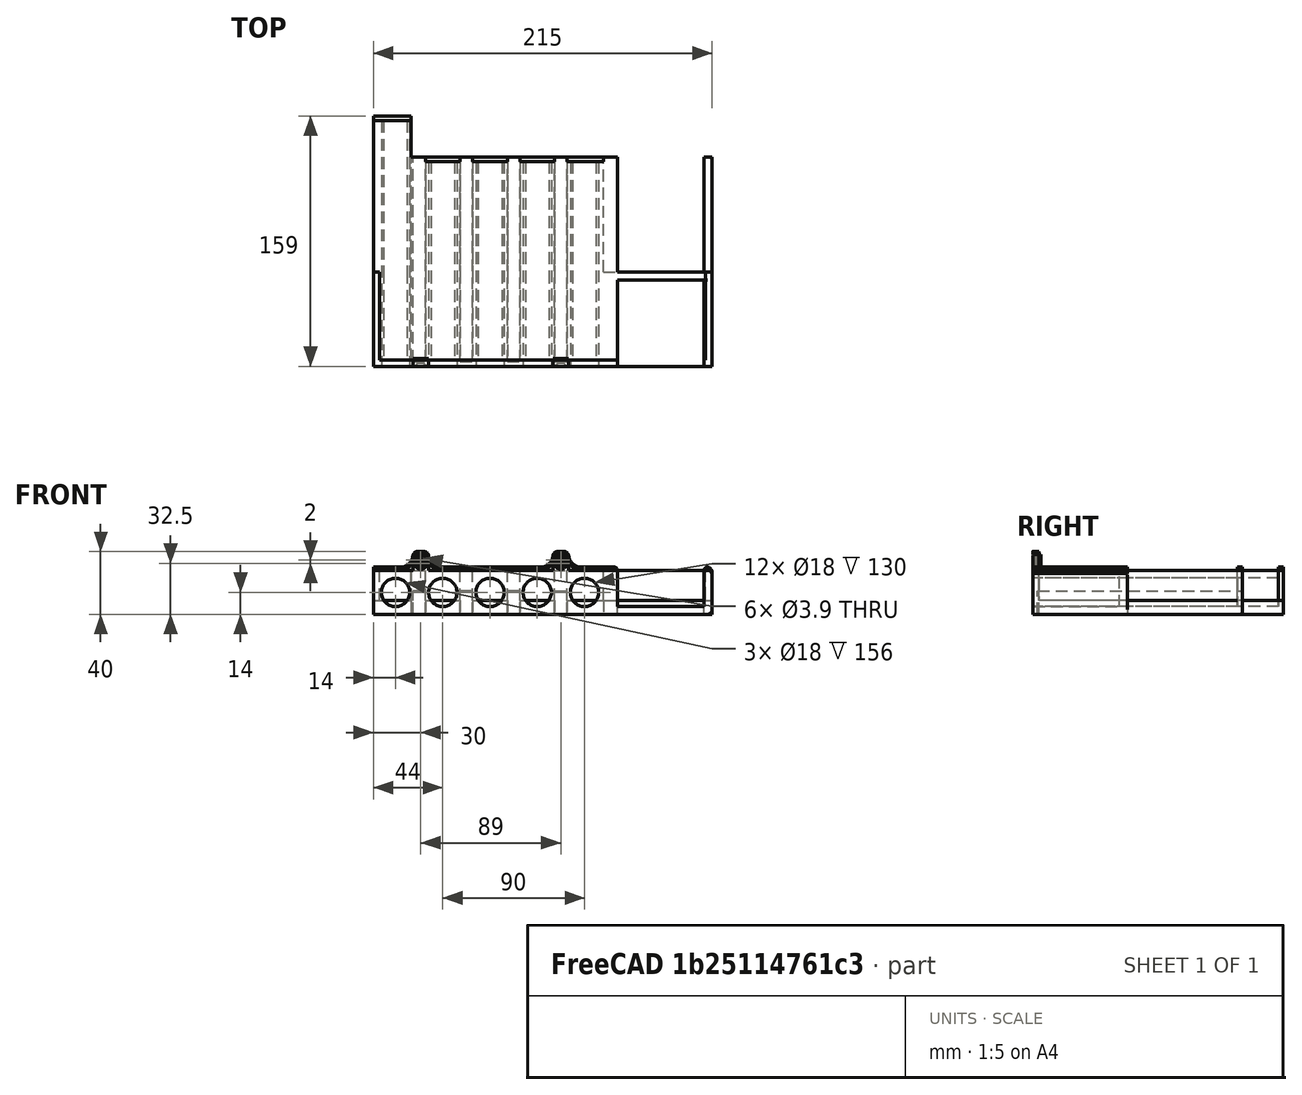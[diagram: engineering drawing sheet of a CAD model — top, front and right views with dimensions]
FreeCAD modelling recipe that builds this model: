
FCSTD DOCUMENT  (FreeCAD 0.20R29177 (Git))
Label: sujeta_lapices_cinta_metrica
License: All rights reserved
LicenseURL: http://en.wikipedia.org/wiki/All_rights_reserved
objects: Part::Box×19, Part::Cut×18, Part::Fillet×7, Part::Cylinder×5, Part::Feature×5, Part::MultiFuse×3, Sketcher::SketchObject×2, Mesh::Feature×2, PartDesign::Pad×1, PartDesign::Hole×1, PartDesign::Body×1, Part::Refine×1
note: 65 computed .brp shape members not serialized (recipe doc carries the construction recipe); baked Part::Feature solids carry a one-line shape summary decoded from their .brp

FEATURE [Part::Box] Box  label="Cube"
  AttacherType = Attacher::AttachEngine3D
  Height = 28
  Length = 215
  Width = 159
FEATURE [Part::Cylinder] Cylinder
  Angle = 360
  AttacherType = Attacher::AttachEngine3D
  FirstAngle = 0
  Height = 156
  Placement = pos=(14,156,14) rot=(1,0,0;1.5708rad)
  Radius = 9
  SecondAngle = 0
FEATURE [Part::Cylinder] Cylinder001 .. Cylinder004  x4 (patterned run collapsed; names and placements below)
  Angle = 360
  AttacherType = Attacher::AttachEngine3D
  FirstAngle = 0
  Height = 130
  Radius = 9
  SecondAngle = 0
  placements: 4 in arithmetic series — first pos=(44,130,14) rot=(1,0,0;1.5708rad), step (30,0,0), last pos=(134,130,14) rot=(1,0,0;1.5708rad)
FEATURE [Part::Box] Box001  label="Cube001"
  AttacherType = Attacher::AttachEngine3D
  Height = 23
  Length = 55
  Placement = pos=(155,0,5) rot=(0,0,1;0rad)
  Width = 55
FEATURE [Part::Box] Box002  label="Cube002"
  AttacherType = Attacher::AttachEngine3D
  Height = 34
  Length = 55
  Placement = pos=(155,60,-3) rot=(0,0,1;0rad)
  Width = 103
FEATURE [Part::Box] Box003  label="Cube003"
  AttacherType = Attacher::AttachEngine3D
  Height = 33
  Length = 197
  Placement = pos=(24,133,-3) rot=(0,0,1;0rad)
  Width = 103
FEATURE [Part::Box] Box004  label="Cube004"
  AttacherType = Attacher::AttachEngine3D
  Height = 15
  Length = 8
  Placement = pos=(25,3,0) rot=(0,0,1;0rad)
  Width = 165
FEATURE [Part::Box] Box005  label="Cube005"
  AttacherType = Attacher::AttachEngine3D
  Height = 15
  Length = 8
  Placement = pos=(55,3,0) rot=(0,0,1;0rad)
  Width = 165
FEATURE [Part::Box] Box006  label="Cube006"
  AttacherType = Attacher::AttachEngine3D
  Height = 15
  Length = 8
  Placement = pos=(85,3,0) rot=(0,0,1;0rad)
  Width = 165
FEATURE [Part::Box] Box007  label="Cube007"
  AttacherType = Attacher::AttachEngine3D
  Height = 15
  Length = 8
  Placement = pos=(115,3,0) rot=(0,0,1;0rad)
  Width = 165
FEATURE [Part::Cut] Cut
  Base = -> Box
  Tool = -> Box001
FEATURE [Part::Cut] Cut001
  Base = -> Cut
  Tool = -> Box002
FEATURE [Part::Cut] Cut002
  Base = -> Cut001
  Tool = -> Box003
FEATURE [Part::Cut] Cut003
  Base = -> Cut002
  Tool = -> Box004
FEATURE [Part::Cut] Cut004
  Base = -> Cut003
  Tool = -> Box005
FEATURE [Part::Cut] Cut005
  Base = -> Cut004
  Tool = -> Box006
FEATURE [Part::Cut] Cut006
  Base = -> Cut005
  Tool = -> Box007
FEATURE [Part::Cut] Cut007
  Base = -> Cut006
  Tool = -> Cylinder
FEATURE [Part::Cut] Cut008
  Base = -> Cut007
  Tool = -> Cylinder001
FEATURE [Part::Cut] Cut009
  Base = -> Cut008
  Tool = -> Cylinder002
FEATURE [Part::Cut] Cut010
  Base = -> Cut009
  Tool = -> Cylinder003
FEATURE [Part::Cut] Cut011
  Base = -> Cut010
  Tool = -> Cylinder004
FEATURE [Sketcher::SketchObject] Sketch
  FullyConstrained = true
  MapMode = 5
  Placement = pos=(0,0,0) rot=(1,0,0;1.5708rad)
  Support = -> [XZ_Plane]
  sketch-geometry (10):
    g0: LineSegment StartX=25 StartY=38 StartZ=0 EndX=35 EndY=38 EndZ=0
    g1: LineSegment StartX=35 StartY=38 StartZ=0 EndX=35 EndY=28 EndZ=0
    g2: LineSegment StartX=35 StartY=27 StartZ=0 EndX=25 EndY=27 EndZ=0
    g3: LineSegment StartX=25 StartY=27 StartZ=0 EndX=25 EndY=38 EndZ=0
    g4: LineSegment StartX=114 StartY=38 StartZ=0 EndX=124 EndY=38 EndZ=0
    g5: LineSegment StartX=124 StartY=38 StartZ=0 EndX=124 EndY=27 EndZ=0
    g6: LineSegment StartX=124 StartY=27 StartZ=0 EndX=114 EndY=27 EndZ=0
    g7: LineSegment StartX=114 StartY=28 StartZ=0 EndX=114 EndY=38 EndZ=0
    g8: LineSegment StartX=35 StartY=28 StartZ=0 EndX=114 EndY=28 EndZ=0
    g9: LineSegment StartX=114 StartY=27 StartZ=0 EndX=35 EndY=27 EndZ=0
  constraints (30):
    c: Coincident(g0,g1)
    c: Coincident(g2,g3)
    c: Coincident(g3,g0)
    c: Horizontal(g0)
    c: Horizontal(g2)
    c: Vertical(g1)
    c: Vertical(g3)
    c: Coincident(g4,g5)
    c: Coincident(g5,g6)
    c: Coincident(g7,g4)
    c: Horizontal(g4)
    c: Horizontal(g6)
    c: Vertical(g5)
    c: Vertical(g7)
    c: DistanceX(g0,g0) = 10
    c: DistanceX(g-1,g2) = 25
    c: Horizontal(g0,g4)
    c: DistanceY(g-1,g2) = 27
    c: DistanceX(g0,g4) = 79
    c: Equal(g0,g4)
    c: DistanceY(g2,g1) = 11
    c: Horizontal(g8)
    c: Coincident(g9,g6)
    c: Coincident(g9,g2)
    c: DistanceY(g2,g8) = 1
    c: Coincident(g1,g8)
    c: Coincident(g7,g8)
    c: Horizontal(g9)
    c: Equal(g6,g4)
    c: Equal(g8,g9)
FEATURE [PartDesign::Pad] Pad
  Direction = (1,1,1)
  Length = 5
  Length2 = 100
  Placement = pos=(0,0,0) rot=(1,0,0;1.5708rad)
  Profile = -> Sketch
  Type = 0
FEATURE [Sketcher::SketchObject] Sketch001
  ExternalGeometry = -> [Pad]
  FullyConstrained = true
  MapMode = 5
  Placement = pos=(0,-5,2.2e-15) rot=(1,0,0;1.5708rad)
  Support = -> [Pad]
  sketch-geometry (2):
    g0: Circle CenterX=30 CenterY=32.5 CenterZ=0 NormalX=0 NormalY=0 NormalZ=1 AngleXU=0 Radius=2
    g1: Circle CenterX=119 CenterY=32.5 CenterZ=0 NormalX=0 NormalY=0 NormalZ=1 AngleXU=0 Radius=2
  constraints (4):
    c: Equal(g0,g1)
    c: Symmetric(g-3,g-4,g0)
    c: Symmetric(g-5,g-6,g1)
    c: Radius(g1) = 2
FEATURE [PartDesign::Hole] Hole
  BaseFeature = -> Pad
  CustomThreadClearance = 0
  Depth = 25
  DepthType = 0
  Diameter = 3.9
  DrillForDepth = false
  DrillPoint = 1
  DrillPointAngle = 118
  HoleCutCountersinkAngle = 90
  HoleCutCustomValues = false
  HoleCutDepth = 0
  HoleCutDiameter = 7.8
  HoleCutType = 4
  ModelThread = false
  Placement = pos=(0,0,0) rot=(1,0,0;1.5708rad)
  Profile = -> Sketch001
  Tapered = false
  TaperedAngle = 90
  ThreadClass = 0
  ThreadDepth = 23.5
  ThreadDepthType = 0
  ThreadDirection = 0
  ThreadFit = 0
  ThreadSize = 10
  ThreadType = 1
  Threaded = false
  UseCustomThreadClearance = false
FEATURE [PartDesign::Body] Body
  Group = -> [Sketch,Pad,Sketch001,Hole]
  Origin = -> Origin
  Placement = pos=(0,5,0) rot=(0,0,1;0rad)
  Tip = -> Hole
FEATURE [Part::MultiFuse] Fusion
  Shapes = -> [Body,Cut011]
FEATURE [Part::Feature] Fusion001
  shape: bbox 215 x 159 x 38 mm, 58 faces (baked)
FEATURE [Part::Feature] Fusion001_solid  label="Fusion001 (Solid)"
  shape: bbox 215 x 159 x 38 mm, 58 faces (baked)
FEATURE [Part::Refine] Fusion001_solid001  label="Fusion001 (Solid)001"
  Source = -> Fusion001_solid
FEATURE [Part::Fillet] Fillet
  Base = -> Fusion001_solid001
  Edges = 2 edges r=3: [Edge1,Edge2]
FEATURE [Part::Fillet] Fillet001
  Base = -> Fillet
  Edges = 2 edges r=3: [Edge83,Edge87]
FEATURE [Part::Fillet] Fillet002
  Base = -> Fillet001
  Edges = 2 edges r=8: [Edge35,Edge37]
FEATURE [Part::Fillet] Fillet003
  Base = -> Fillet002
  Edges = 2 edges r=8: [Edge39,Edge43]
FEATURE [Part::Fillet] Fillet004
  Base = -> Fillet003
  Edges = 2 edges r=1: [Edge38,Edge42]
FEATURE [Part::Fillet] Fillet005
  Base = -> Fillet004
  Edges = 2 edges r=3: [Edge40,Edge73]
FEATURE [Part::Fillet] Fillet006
  Base = -> Fillet005
  Edges = 2 edges r=3: [Edge47,Edge71]
FEATURE [Mesh::Feature] Mesh  label="Fillet002 (Meshed)"
FEATURE [Part::Feature] Fillet006001
  shape: bbox 215 x 159.3 x 38 mm, 69 faces (baked)
FEATURE [Part::Box] Box008  label="Cube008"
  AttacherType = Attacher::AttachEngine3D
  Height = 38
  Length = 207
  Placement = pos=(4,4,9) rot=(0,0,1;0rad)
  Width = 157
FEATURE [Part::Cut] Cut012
  Base = -> Fillet006001
  Tool = -> Box008
FEATURE [Part::Box] Box009  label="Cube009"
  AttacherType = Attacher::AttachEngine3D
  Height = 36
  Length = 8
  Placement = pos=(24,4,0) rot=(0,0,1;0rad)
  Width = 148
FEATURE [Part::Cut] Cut013
  Base = -> Cut012
  Tool = -> Box009
FEATURE [Part::Box] Box010  label="Cube010"
  AttacherType = Attacher::AttachEngine3D
  Height = 36
  Length = 219
  Placement = pos=(-2,60,9) rot=(0,0,1;0rad)
  Width = 126
FEATURE [Part::Cut] Cut014
  Base = -> Cut013
  Tool = -> Box010
FEATURE [Part::Feature] Cut014001
  shape: bbox 215 x 159.3 x 38 mm, 101 faces (baked)
FEATURE [Part::Box] Box011  label="Cube011"
  AttacherType = Attacher::AttachEngine3D
  Height = 24
  Length = 221
  Placement = pos=(-3,0,0) rot=(0,0,1;0rad)
  Width = 168
FEATURE [Part::Feature] Cut014001001
  shape: bbox 215 x 159.3 x 38 mm, 101 faces (baked)
FEATURE [Part::Box] Box012  label="Cube012"
  AttacherType = Attacher::AttachEngine3D
  Height = 26
  Length = 221
  Placement = pos=(-3,-3,28) rot=(0,0,1;0rad)
  Width = 168
FEATURE [Part::Cut] Cut014001002
  Base = -> Cut014001
  Placement = pos=(0,0,2) rot=(0,0,1;0rad)
  Tool = -> Box011
FEATURE [Part::Cut] Cut014001003
  Base = -> Cut014001001
  Tool = -> Box012
FEATURE [Part::MultiFuse] Fusion002
  Shapes = -> [Cut014001002,Cut014001003]
FEATURE [Part::Box] Box013  label="Cube013"
  AttacherType = Attacher::AttachEngine3D
  Height = 10
  Length = 76
  Placement = pos=(146,60,0) rot=(0,0,1;0rad)
  Width = 119
FEATURE [Part::Cut] Cut014001004
  Base = -> Fusion002
  Tool = -> Box013
FEATURE [Part::Box] Box014  label="Cube014"
  AttacherType = Attacher::AttachEngine3D
  Height = 21
  Length = 23
  Placement = pos=(123,130,9) rot=(0,0,1;0rad)
  Width = 3
FEATURE [Part::Box] Box015  label="Cube015"
  AttacherType = Attacher::AttachEngine3D
  Height = 21
  Length = 22
  Placement = pos=(93,130,9) rot=(0,0,1;0rad)
  Width = 3
FEATURE [Part::Box] Box016  label="Cube016"
  AttacherType = Attacher::AttachEngine3D
  Height = 21
  Length = 22
  Placement = pos=(63,130,9) rot=(0,0,1;0rad)
  Width = 3
FEATURE [Part::Box] Box017  label="Cube017"
  AttacherType = Attacher::AttachEngine3D
  Height = 21
  Length = 22
  Placement = pos=(33,130,9) rot=(0,0,1;0rad)
  Width = 3
FEATURE [Part::Box] Box018  label="Cube018"
  AttacherType = Attacher::AttachEngine3D
  Height = 21
  Length = 24
  Placement = pos=(0,156,9) rot=(0,0,1;0rad)
  Width = 3
FEATURE [Part::MultiFuse] Fusion003  label="modelo3"
  Shapes = -> [Cut014001004,Box014,Box015,Box016,Box017,Box018]
FEATURE [Mesh::Feature] Mesh001  label="modelo004"
